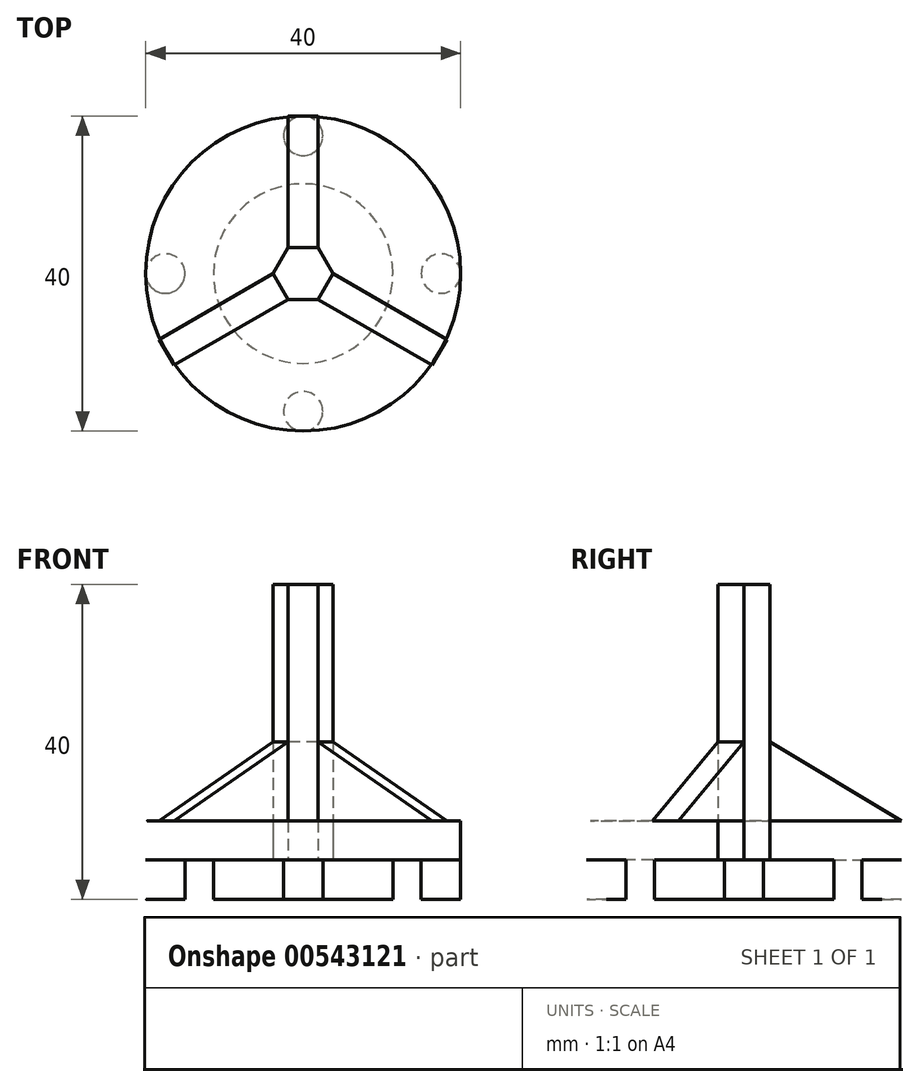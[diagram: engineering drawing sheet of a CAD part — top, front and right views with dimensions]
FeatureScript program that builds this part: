
annotation { "Feature Type Name" : "Feature", "Feature Type Description" : "" }
export const myFeature = defineFeature(function(context is Context, id is Id, definition is map)
    precondition{}
    {
        {
            var Q0;
            Q0=qCreatedBy(makeId("Top.planeOp"),FACE);
            var sketch = newSketch(context, id + "F0", { "sketchPlane" : qUnion([Q0])});
            skCircle(sketch, "E0", {"center": v(0, 0) * mm, "radius": 20 * mm});
            skCircle(sketch, "E1", {"center": v(0, 17.5) * mm, "radius": 2.5 * mm});
            skPoint(sketch, "E1.second.point", {"position": v(0, 15) * mm});
            skPoint(sketch, "E1.third.point", {"position": v(-2.28, 18.52) * mm});
            skCircle(sketch, "E2.1.0", {"center": v(-17.5, 0) * mm, "radius": 2.5 * mm});
            skPoint(sketch, "E2.1.1", {"position": v(-15, 0) * mm});
            skPoint(sketch, "E2.1.2", {"position": v(-18.52, -2.28) * mm});
            skCircle(sketch, "E2.2.0", {"center": v(0, -17.5) * mm, "radius": 2.5 * mm});
            skPoint(sketch, "E2.2.1", {"position": v(0, -15) * mm});
            skPoint(sketch, "E2.2.2", {"position": v(2.28, -18.52) * mm});
            skCircle(sketch, "E3", {"center": v(0, 0) * mm, "radius": 11.4 * mm});
            skCircle(sketch, "E4.cCircle", {"center": v(0, 0) * mm, "radius": 3.3 * mm, "construction": true});
            skLineSegment(sketch, "E4.0", {"start": v(-1.9, 3.3) * mm, "end": v(1.9, 3.3) * mm});
            skLineSegment(sketch, "E4.1", {"start": v(1.9, 3.3) * mm, "end": v(3.81, 0) * mm});
            skLineSegment(sketch, "E4.2", {"start": v(3.81, 0) * mm, "end": v(1.9, -3.3) * mm});
            skLineSegment(sketch, "E4.3", {"start": v(1.9, -3.3) * mm, "end": v(-1.9, -3.3) * mm});
            skLineSegment(sketch, "E4.4", {"start": v(-1.9, -3.3) * mm, "end": v(-3.81, 0) * mm});
            skLineSegment(sketch, "E4.5", {"start": v(-3.81, 0) * mm, "end": v(-1.9, 3.3) * mm});
            skPoint(sketch, "E4.0.midPoint", {"position": v(0, 3.3) * mm});
            skPoint(sketch, "E5.0.3.0", {"position": v(15, 0) * mm});
            skCircle(sketch, "E5.2.3.0", {"center": v(17.5, 0) * mm, "radius": 2.5 * mm});
            skPoint(sketch, "E5.3.3.0", {"position": v(18.52, 2.28) * mm});
            skSolve(sketch);
        }
        {
            var Q0;
            {var subQ7=sQuery(id+"F0.wireOp",EDGE,"E1");Q0=makeQuery(id+"F0.imprint","IMPRINT",FACE,{"disambiguationData":[TD([[makeQuery(id+"F0.imprint","IMPRINT",EDGE,{"derivedFrom":subQ7}),-1.0]])]});}
            var Q1;
            Q1=makeQuery(id+"F0.imprint","IMPRINT",FACE,{"disambiguationData":[TD([[makeQuery(id+"F0.imprint","IMPRINT",EDGE,{"derivedFrom":sQuery(id+"F0.wireOp",EDGE,"E2.1.0")}),1.0]])]});
            var Q2;
            Q2=makeQuery(id+"F0.imprint","IMPRINT",FACE,{"disambiguationData":[TD([[makeQuery(id+"F0.imprint","IMPRINT",EDGE,{"derivedFrom":sQuery(id+"F0.wireOp",EDGE,"E3")}),1.0]])]});
            var Q3;
            Q3=makeQuery(id+"F0.imprint","IMPRINT",FACE,{"disambiguationData":[TD([[makeQuery(id+"F0.imprint","IMPRINT",EDGE,{"derivedFrom":sQuery(id+"F0.wireOp",EDGE,"E2.3.0")}),1.0]])]});
            var Q4;
            Q4=makeQuery(id+"F0.imprint","IMPRINT",FACE,{"disambiguationData":[TD([[makeQuery(id+"F0.imprint","IMPRINT",EDGE,{"derivedFrom":sQuery(id+"F0.wireOp",EDGE,"E1")}),1.0]])]});
            var Q5;
            Q5=makeQuery(id+"F0.imprint","IMPRINT",FACE,{"disambiguationData":[TD([[makeQuery(id+"F0.imprint","IMPRINT",EDGE,{"derivedFrom":sQuery(id+"F0.wireOp",EDGE,"E2.2.0")}),1.0]])]});
            var Q6;
            Q6=makeQuery(id+"F0.imprint","IMPRINT",FACE,{"disambiguationData":[TD([[makeQuery(id+"F0.imprint","IMPRINT",EDGE,{"derivedFrom":sQuery(id+"F0.wireOp",EDGE,"E5.2.3.0")}),1.0]])]});
            extrude(context, id + "F1", {"entities" : qUnion([Q0, Q1, Q2, Q3, Q4, Q5, Q6]), "depth" : 5 * mm, "offsetDistance" : 25 * mm});
        }
        {
            var Q0;
            Q0=makeQuery(id+"F0.imprint","IMPRINT",FACE,{"disambiguationData":[TD([[makeQuery(id+"F0.imprint","IMPRINT",EDGE,{"derivedFrom":sQuery(id+"F0.wireOp",EDGE,"E3")}),1.0]])]});
            var Q1;
            Q1=makeQuery(id+"F0.imprint","IMPRINT",FACE,{"disambiguationData":[TD([[makeQuery(id+"F0.imprint","IMPRINT",EDGE,{"derivedFrom":sQuery(id+"F0.wireOp",EDGE,"E4.0")}),-1.0]])]});
            extrude(context, id + "F2", {"entities" : qUnion([Q0, Q1]), "operationType" : NewBodyOperationType.ADD, "oppositeDirection" : true, "depth" : 5 * mm, "offsetDistance" : 25 * mm});
        }
        {
            var Q0;
            Q0=makeQuery(id+"F0.imprint","IMPRINT",FACE,{"disambiguationData":[TD([[makeQuery(id+"F0.imprint","IMPRINT",EDGE,{"derivedFrom":sQuery(id+"F0.wireOp",EDGE,"E2.1.0")}),1.0]])]});
            var Q1;
            Q1=makeQuery(id+"F0.imprint","IMPRINT",FACE,{"disambiguationData":[TD([[makeQuery(id+"F0.imprint","IMPRINT",EDGE,{"derivedFrom":sQuery(id+"F0.wireOp",EDGE,"E2.3.0")}),1.0]])]});
            var Q2;
            Q2=makeQuery(id+"F0.imprint","IMPRINT",FACE,{"disambiguationData":[TD([[makeQuery(id+"F0.imprint","IMPRINT",EDGE,{"derivedFrom":sQuery(id+"F0.wireOp",EDGE,"E2.2.0")}),1.0]])]});
            var Q3;
            Q3=makeQuery(id+"F0.imprint","IMPRINT",FACE,{"disambiguationData":[TD([[makeQuery(id+"F0.imprint","IMPRINT",EDGE,{"derivedFrom":sQuery(id+"F0.wireOp",EDGE,"E1")}),1.0]])]});
            var Q4;
            Q4=makeQuery(id+"F0.imprint","IMPRINT",FACE,{"disambiguationData":[TD([[makeQuery(id+"F0.imprint","IMPRINT",EDGE,{"derivedFrom":sQuery(id+"F0.wireOp",EDGE,"E5.2.3.0")}),1.0]])]});
            extrude(context, id + "F3", {"entities" : qUnion([Q0, Q1, Q2, Q3, Q4]), "operationType" : NewBodyOperationType.ADD, "oppositeDirection" : true, "depth" : 5 * mm, "offsetDistance" : 25 * mm});
        }
        {
            var Q0;
            Q0=makeQuery(id+"F0.imprint","IMPRINT",FACE,{"disambiguationData":[TD([[makeQuery(id+"F0.imprint","IMPRINT",EDGE,{"derivedFrom":sQuery(id+"F0.wireOp",EDGE,"E4.0")}),-1.0]])]});
            extrude(context, id + "F4", {"entities" : qUnion([Q0]), "depth" : 35 * mm, "offsetDistance" : 25 * mm});
        }
        {
            var Q0;
            Q0=qCreatedBy(makeId("Right.planeOp"),FACE);
            var sketch = newSketch(context, id + "F5", { "sketchPlane" : qUnion([Q0])});
            skLineSegment(sketch, "E6.0", {"start": v(3.3, 35) * mm, "end": v(3.3, 0) * mm});
            skLineSegment(sketch, "E7.0", {"start": v(-20, 5) * mm, "end": v(20, 5) * mm});
            skLineSegment(sketch, "E8", {"start": v(3.3, 5) * mm, "end": v(3.3, 15) * mm});
            skLineSegment(sketch, "E9", {"start": v(3.3, 15) * mm, "end": v(20, 5) * mm});
            skLineSegment(sketch, "E10", {"start": v(3.3, 5) * mm, "end": v(20, 5) * mm});
            skLineSegment(sketch, "E11", {"start": v(3.3, 15) * mm, "end": v(3.3, 5) * mm});
            skLineSegment(sketch, "E12", {"start": v(0, 0) * mm, "end": v(0, 20.42) * mm, "construction": true});
            skSolve(sketch);
        }
        {
            var Q0;
            Q0=makeQuery(id+"F5.imprint","IMPRINT",FACE,{"disambiguationData":[TD([[makeQuery(id+"F5.imprint","IMPRINT",EDGE,{"derivedFrom":sQuery(id+"F5.wireOp",EDGE,"E9")}),-1.0]])]});
            extrude(context, id + "F6", {"entities" : qUnion([Q0]), "depth" : 1.9 * mm, "offsetDistance" : 25 * mm, "hasSecondDirection" : true, "secondDirectionOppositeDirection" : true, "secondDirectionDepth" : 1.9 * mm});
        }
        {
            var Q0;
            Q0=makeQuery(id+"F6.opExtrude","SWEPT_BODY",BODY,{"disambiguationData":[OSD([sQuery(id+"F5.wireOp",EDGE,"E9"),sQuery(id+"F5.wireOp",EDGE,"E10"),sQuery(id+"F5.wireOp",EDGE,"E11")])]});
            var Q1;
            Q1=sQuery(id+"F5.wireOp",EDGE,"E12");
            circularPattern(context, id + "F7", {"entities" : qUnion([Q0]), "axis" : qUnion([Q1]), "angle" : 360 * degree, "instanceCount" : 3, "equalSpace" : true});
        }
    });
